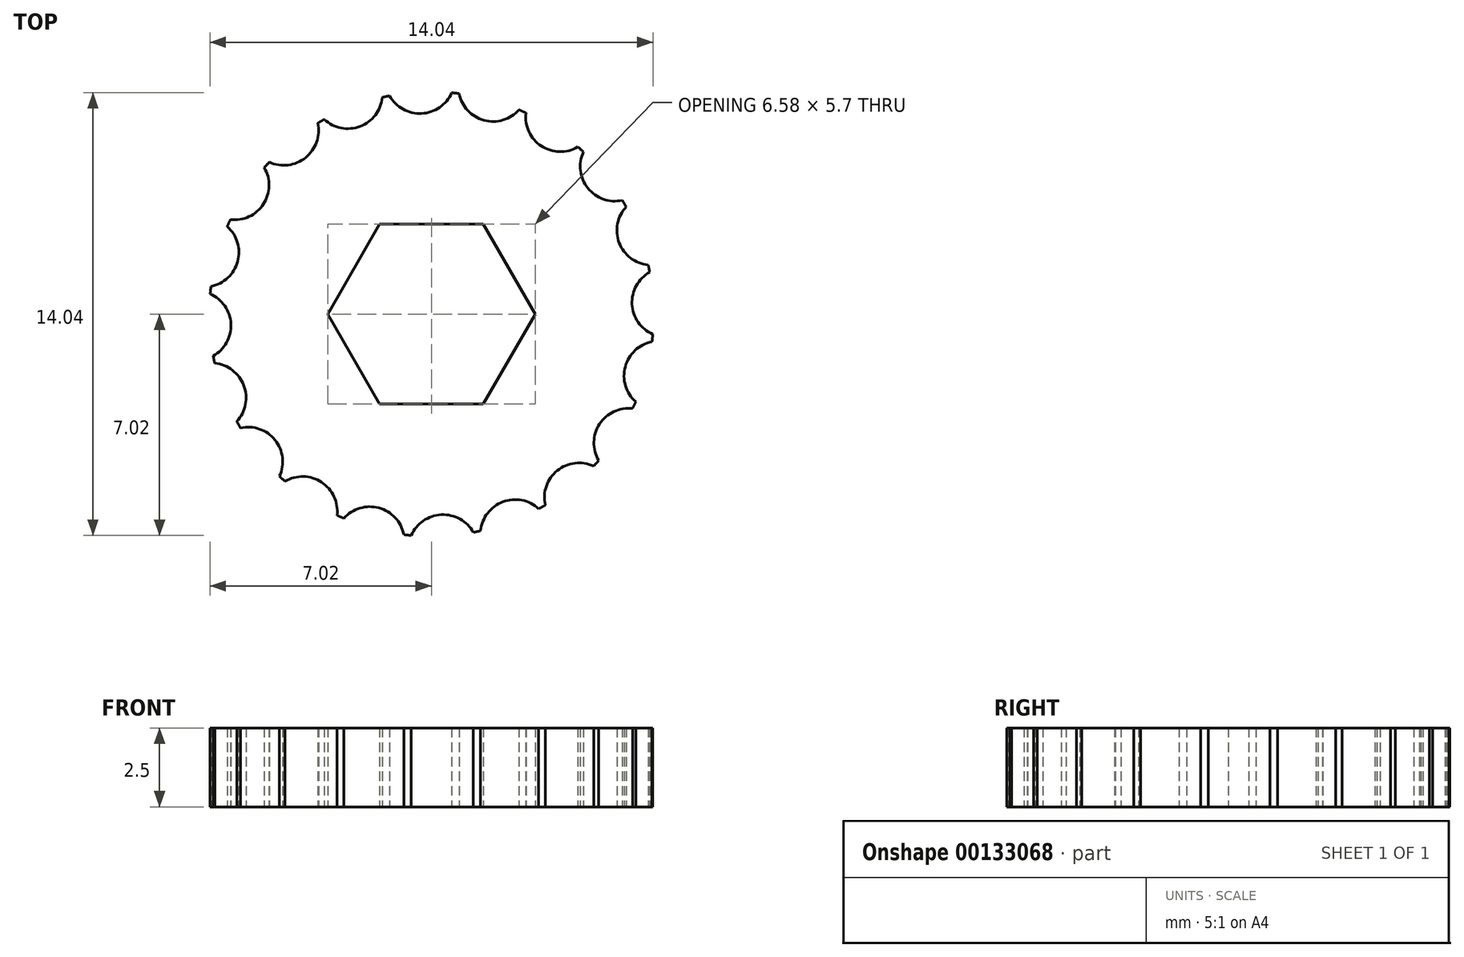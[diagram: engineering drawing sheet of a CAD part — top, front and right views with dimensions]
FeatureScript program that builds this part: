
annotation { "Feature Type Name" : "Feature", "Feature Type Description" : "" }
export const myFeature = defineFeature(function(context is Context, id is Id, definition is map)
    precondition{}
    {
        {
            var Q0;
            Q0=qCreatedBy(makeId("Top.planeOp"),FACE);
            var sketch = newSketch(context, id + "F0", { "sketchPlane" : qUnion([Q0])});
            skArc(sketch, "E0", {"start": v(-6.38, 3) * mm, "mid": v(-6.43, 2.89) * mm, "end": v(-6.48, 2.78) * mm});
            skPoint(sketch, "E1.0.midPoint", {"position": v(0, 2.14) * mm});
            skArc(sketch, "E2", {"start": v(-6.38, 3) * mm, "mid": v(-5.33, 3.48) * mm, "end": v(-5.3, 4.64) * mm});
            skArc(sketch, "E3.1.0", {"start": v(-7, 0.88) * mm, "mid": v(-6.14, 1.67) * mm, "end": v(-6.48, 2.78) * mm});
            skArc(sketch, "E3.2.0", {"start": v(-6.92, -1.33) * mm, "mid": v(-6.36, -0.31) * mm, "end": v(-7.02, 0.64) * mm});
            skArc(sketch, "E3.3.0", {"start": v(-6.17, -3.4) * mm, "mid": v(-5.95, -2.26) * mm, "end": v(-6.87, -1.56) * mm});
            skArc(sketch, "E3.4.0", {"start": v(-4.82, -5.14) * mm, "mid": v(-4.96, -4) * mm, "end": v(-6.05, -3.6) * mm});
            skArc(sketch, "E3.5.0", {"start": v(-3, -6.38) * mm, "mid": v(-3.48, -5.33) * mm, "end": v(-4.64, -5.3) * mm});
            skArc(sketch, "E3.6.0", {"start": v(-0.88, -7) * mm, "mid": v(-1.67, -6.14) * mm, "end": v(-2.78, -6.48) * mm});
            skArc(sketch, "E3.7.0", {"start": v(1.33, -6.92) * mm, "mid": v(0.31, -6.36) * mm, "end": v(-0.64, -7.02) * mm});
            skArc(sketch, "E3.8.0", {"start": v(3.4, -6.17) * mm, "mid": v(2.26, -5.95) * mm, "end": v(1.56, -6.87) * mm});
            skArc(sketch, "E3.9.0", {"start": v(5.14, -4.82) * mm, "mid": v(4, -4.96) * mm, "end": v(3.6, -6.05) * mm});
            skArc(sketch, "E3.10.0", {"start": v(6.38, -3) * mm, "mid": v(5.33, -3.48) * mm, "end": v(5.3, -4.64) * mm});
            skArc(sketch, "E3.11.0", {"start": v(7, -0.88) * mm, "mid": v(6.14, -1.67) * mm, "end": v(6.48, -2.78) * mm});
            skArc(sketch, "E3.12.0", {"start": v(6.92, 1.33) * mm, "mid": v(6.36, 0.31) * mm, "end": v(7.02, -0.64) * mm});
            skArc(sketch, "E3.13.0", {"start": v(6.17, 3.4) * mm, "mid": v(5.95, 2.26) * mm, "end": v(6.87, 1.56) * mm});
            skArc(sketch, "E3.14.0", {"start": v(4.82, 5.14) * mm, "mid": v(4.96, 4) * mm, "end": v(6.05, 3.6) * mm});
            skArc(sketch, "E3.15.0", {"start": v(3, 6.38) * mm, "mid": v(3.48, 5.33) * mm, "end": v(4.64, 5.3) * mm});
            skArc(sketch, "E3.16.0", {"start": v(0.88, 7) * mm, "mid": v(1.67, 6.14) * mm, "end": v(2.78, 6.48) * mm});
            skArc(sketch, "E3.17.0", {"start": v(-1.33, 6.92) * mm, "mid": v(-0.31, 6.36) * mm, "end": v(0.64, 7.02) * mm});
            skArc(sketch, "E3.18.0", {"start": v(-3.4, 6.17) * mm, "mid": v(-2.26, 5.95) * mm, "end": v(-1.56, 6.87) * mm});
            skArc(sketch, "E3.19.0", {"start": v(-5.14, 4.82) * mm, "mid": v(-4, 4.96) * mm, "end": v(-3.6, 6.05) * mm});
            skArc(sketch, "E4.trimOffspring", {"start": v(-7, 0.88) * mm, "mid": v(-7, 0.76) * mm, "end": v(-7.02, 0.64) * mm});
            skArc(sketch, "E5.trimOffspring", {"start": v(-6.92, -1.33) * mm, "mid": v(-6.9, -1.44) * mm, "end": v(-6.87, -1.56) * mm});
            skArc(sketch, "E6.trimOffspring", {"start": v(-6.17, -3.4) * mm, "mid": v(-6.11, -3.5) * mm, "end": v(-6.05, -3.6) * mm});
            skArc(sketch, "E7.trimOffspring", {"start": v(-4.82, -5.14) * mm, "mid": v(-4.73, -5.22) * mm, "end": v(-4.64, -5.3) * mm});
            skArc(sketch, "E8.trimOffspring", {"start": v(-3, -6.38) * mm, "mid": v(-2.89, -6.43) * mm, "end": v(-2.78, -6.48) * mm});
            skArc(sketch, "E9.trimOffspring", {"start": v(-0.88, -7) * mm, "mid": v(-0.76, -7) * mm, "end": v(-0.64, -7.02) * mm});
            skArc(sketch, "E10.trimOffspring", {"start": v(1.33, -6.92) * mm, "mid": v(1.44, -6.9) * mm, "end": v(1.56, -6.87) * mm});
            skArc(sketch, "E11.trimOffspring", {"start": v(3.4, -6.17) * mm, "mid": v(3.5, -6.11) * mm, "end": v(3.6, -6.05) * mm});
            skArc(sketch, "E12.trimOffspring", {"start": v(5.14, -4.82) * mm, "mid": v(5.22, -4.73) * mm, "end": v(5.3, -4.64) * mm});
            skArc(sketch, "E13.trimOffspring", {"start": v(6.38, -3) * mm, "mid": v(6.43, -2.89) * mm, "end": v(6.48, -2.78) * mm});
            skArc(sketch, "E14.trimOffspring", {"start": v(7, -0.88) * mm, "mid": v(7, -0.76) * mm, "end": v(7.02, -0.64) * mm});
            skArc(sketch, "E15.trimOffspring", {"start": v(6.92, 1.33) * mm, "mid": v(6.9, 1.44) * mm, "end": v(6.87, 1.56) * mm});
            skArc(sketch, "E16.trimOffspring", {"start": v(6.17, 3.4) * mm, "mid": v(6.11, 3.5) * mm, "end": v(6.05, 3.6) * mm});
            skArc(sketch, "E17.trimOffspring", {"start": v(4.82, 5.14) * mm, "mid": v(4.73, 5.22) * mm, "end": v(4.64, 5.3) * mm});
            skArc(sketch, "E18.trimOffspring", {"start": v(3, 6.38) * mm, "mid": v(2.89, 6.43) * mm, "end": v(2.78, 6.48) * mm});
            skArc(sketch, "E19.trimOffspring", {"start": v(0.88, 7) * mm, "mid": v(0.76, 7) * mm, "end": v(0.64, 7.02) * mm});
            skArc(sketch, "E20.trimOffspring", {"start": v(-1.33, 6.92) * mm, "mid": v(-1.44, 6.9) * mm, "end": v(-1.56, 6.87) * mm});
            skArc(sketch, "E21.trimOffspring", {"start": v(-3.4, 6.17) * mm, "mid": v(-3.5, 6.11) * mm, "end": v(-3.6, 6.05) * mm});
            skArc(sketch, "E22.trimOffspring", {"start": v(-5.14, 4.82) * mm, "mid": v(-5.22, 4.73) * mm, "end": v(-5.3, 4.64) * mm});
            skLineSegment(sketch, "E23.0", {"start": v(-1.65, 2.85) * mm, "end": v(1.65, 2.85) * mm});
            skLineSegment(sketch, "E23.1", {"start": v(1.65, 2.85) * mm, "end": v(3.3, 0) * mm});
            skLineSegment(sketch, "E23.2", {"start": v(3.3, 0) * mm, "end": v(1.65, -2.85) * mm});
            skLineSegment(sketch, "E23.3", {"start": v(1.65, -2.85) * mm, "end": v(-1.65, -2.85) * mm});
            skLineSegment(sketch, "E23.4", {"start": v(-1.65, -2.85) * mm, "end": v(-3.3, 0) * mm});
            skLineSegment(sketch, "E23.5", {"start": v(-3.3, 0) * mm, "end": v(-1.65, 2.85) * mm});
            skPoint(sketch, "E23.0.midPoint", {"position": v(0, 2.85) * mm});
            skSolve(sketch);
        }
        {
            var Q0;
            Q0=makeQuery(id+"F0.imprint","IMPRINT",FACE,{"disambiguationData":[TD([[makeQuery(id+"F0.imprint","IMPRINT",EDGE,{"derivedFrom":sQuery(id+"F0.wireOp",EDGE,"E0")}),1.0]])]});
            extrude(context, id + "F1", {"entities" : qUnion([Q0]), "depth" : 2.5 * mm});
        }
    });
